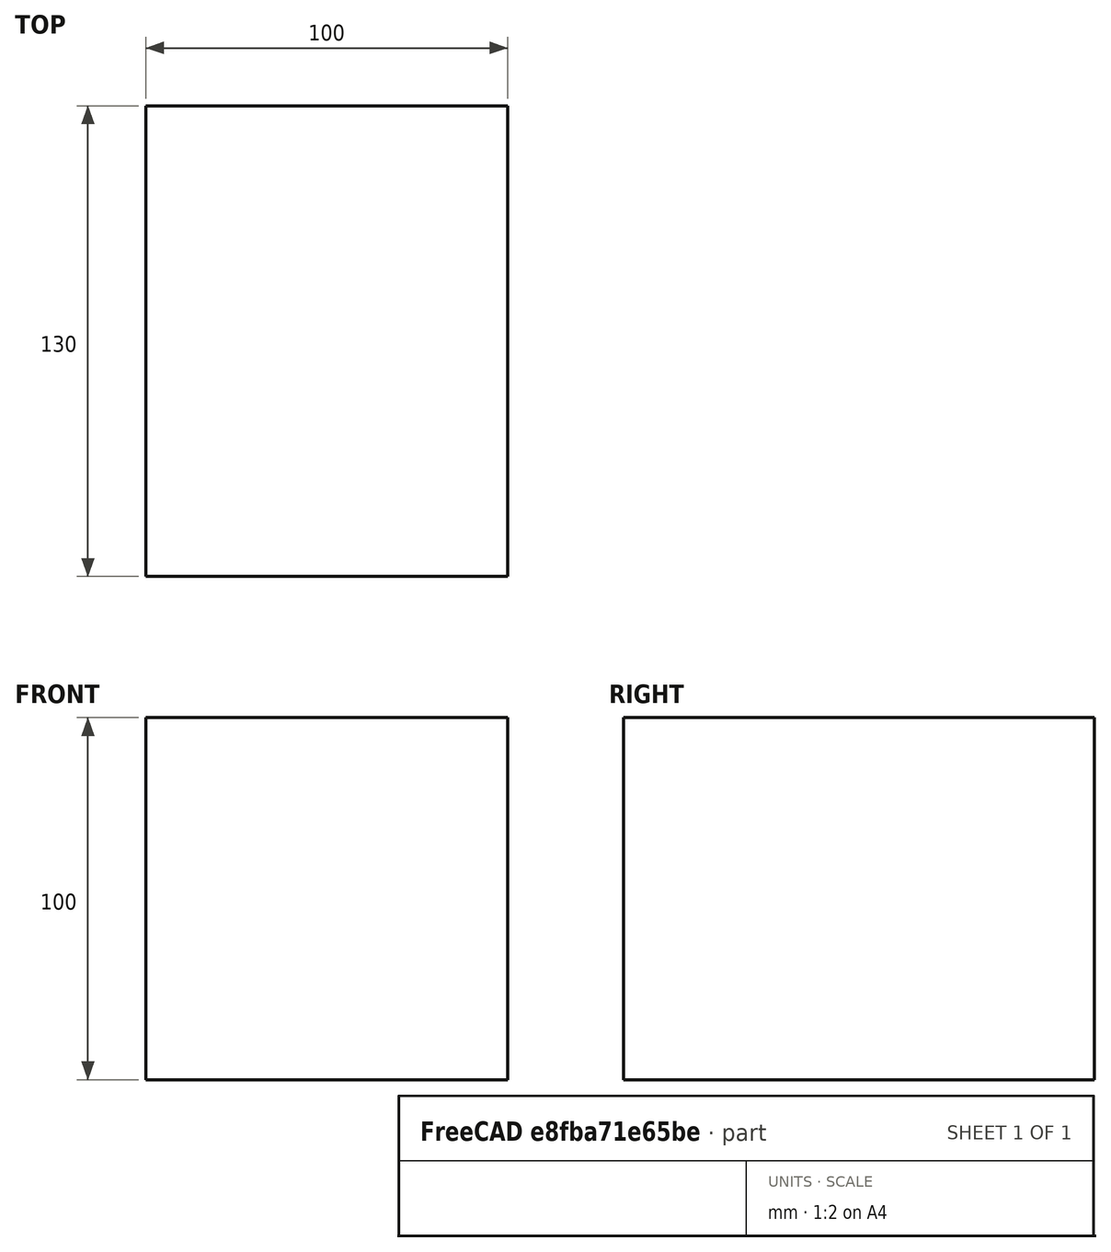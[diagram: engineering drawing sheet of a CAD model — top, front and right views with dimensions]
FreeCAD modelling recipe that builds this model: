
FCSTD DOCUMENT  (FreeCAD 0.15R4671 (Git))
Label: hand_pracsys
License: All rights reserved
LicenseURL: http://en.wikipedia.org/wiki/All_rights_reserved
objects: Part::Part2DObjectPython×5, Part::Extrusion×2
note: 7 computed .brp shape members not serialized (recipe doc carries the construction recipe); baked Part::Feature solids carry a one-line shape summary decoded from their .brp

FEATURE [Part::Part2DObjectPython] Rectangle  # Draft 2D object (typed FeaturePython)
  ChamferSize = 0
  FilletRadius = 0
  Height = 130
  Length = 100
  MakeFace = true
  Placement = pos=(-50,-65,0) rot=(0,0,1;0rad)
FEATURE [Part::Extrusion] Extrude
  Base = -> Rectangle
  Dir = (0,0,100)
  Solid = false
FEATURE [Part::Extrusion] Extrude001
  Base = -> Rectangle
  Dir = (0,0,100)
  Solid = false
FEATURE [Part::Part2DObjectPython] Line  # Draft 2D object (typed FeaturePython)
  ChamferSize = 0
  Closed = true
  End = (60,45.01,220)
  FilletRadius = 0
  Length = 122.577
  MakeFace = true
  Points = (2) [(35,45,100),(60,45.01,220)]
  Start = (35,45,100)
FEATURE [Part::Part2DObjectPython] Line001  # Draft 2D object (typed FeaturePython)
  ChamferSize = 0
  Closed = false
  End = (50,45,220)
  FilletRadius = 0
  Length = 10
  MakeFace = true
  Points = (2) [(60,45,220),(50,45,220)]
  Start = (60,45,220)
FEATURE [Part::Part2DObjectPython] Line002  # Draft 2D object (typed FeaturePython)
  ChamferSize = 0
  Closed = false
  End = (25,45,100)
  FilletRadius = 0
  Length = 122.577
  MakeFace = true
  Points = (2) [(50,45,220),(25,45,100)]
  Start = (50,45,220)
FEATURE [Part::Part2DObjectPython] Line003  # Draft 2D object (typed FeaturePython)
  ChamferSize = 0
  Closed = false
  End = (35,45,100)
  FilletRadius = 0
  Length = 10
  MakeFace = true
  Points = (2) [(25,45,100),(35,45,100)]
  Start = (25,45,100)
